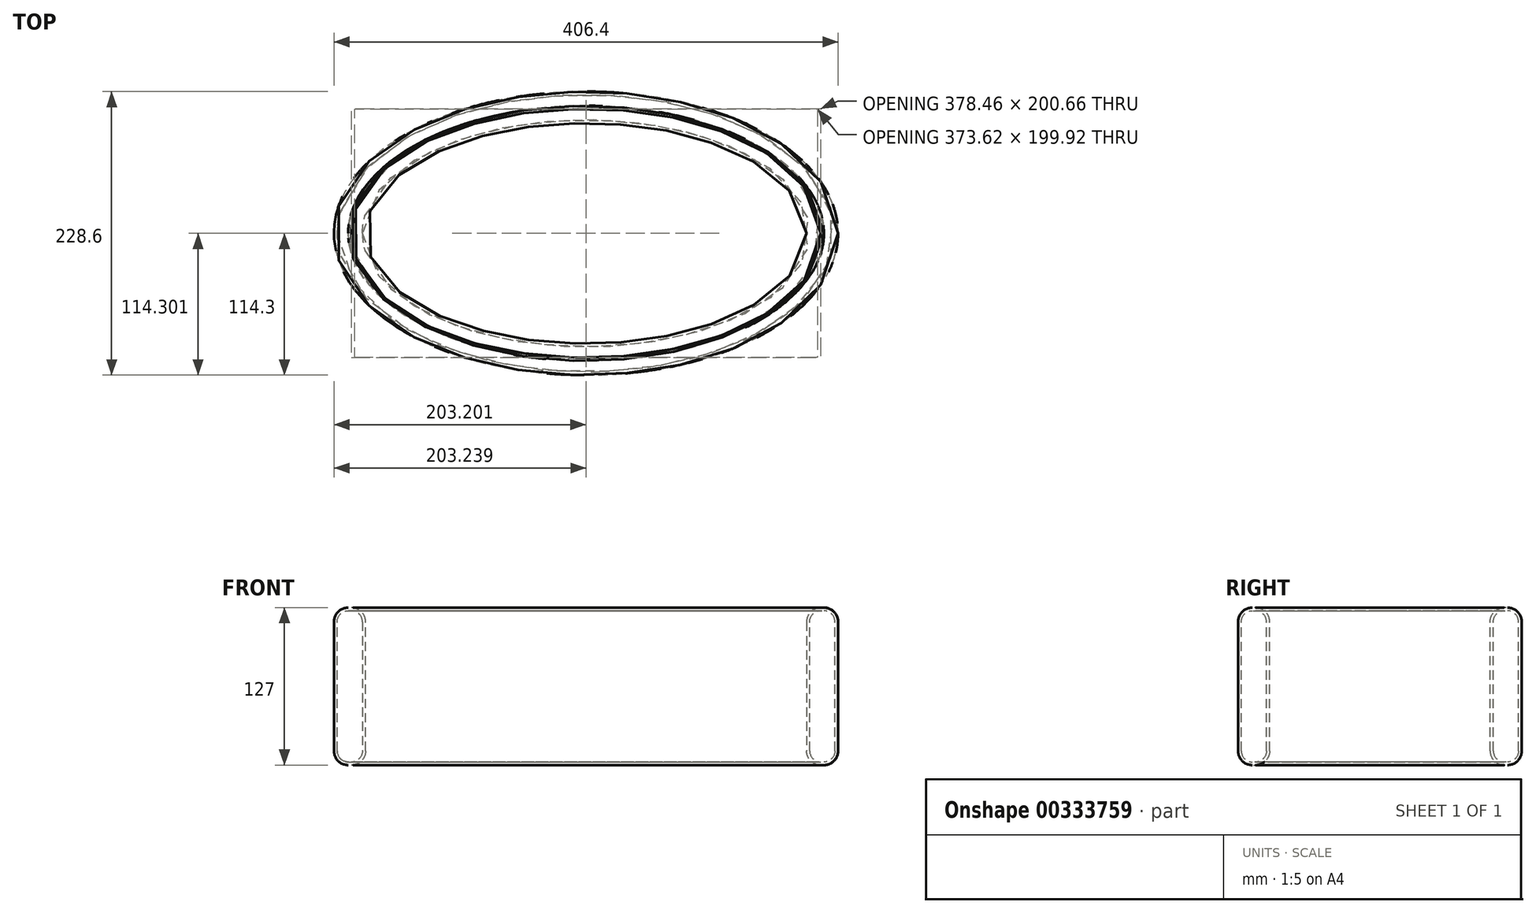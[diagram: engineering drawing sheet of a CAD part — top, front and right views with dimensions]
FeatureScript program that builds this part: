
annotation { "Feature Type Name" : "Feature", "Feature Type Description" : "" }
export const myFeature = defineFeature(function(context is Context, id is Id, definition is map)
    precondition{}
    {
        {
            var Q0;
            Q0=qCreatedBy(makeId("Top.planeOp"),FACE);
            var sketch = newSketch(context, id + "F0", { "sketchPlane" : qUnion([Q0])});
            skEllipse(sketch, "E0", {"center": v(0, 0) * mm, "majorRadius": 177.8 * mm, "minorRadius": 88.9 * mm, "majorAxis": v(1, 0)});
            skEllipse(sketch, "E1", {"center": v(0, 0) * mm, "majorRadius": 203.2 * mm, "minorRadius": 114.3 * mm, "majorAxis": v(1, 0)});
            skSolve(sketch);
        }
        {
            var Q0;
            Q0=makeQuery(id+"F0.imprint","IMPRINT",FACE,{"disambiguationData":[TD([[makeQuery(id+"F0.imprint","IMPRINT",EDGE,{"derivedFrom":sQuery(id+"F0.wireOp",EDGE,"E0")}),-1.0]])]});
            extrude(context, id + "F1", {"entities" : qUnion([Q0]), "depth" : 127 * mm});
        }
        {
            var Q0;
            Q0=makeQuery(id+"F1.opExtrude","CAP_FACE",FACE,{"disambiguationData":[OSD([sQuery(id+"F0.wireOp",EDGE,"E0"),sQuery(id+"F0.wireOp",EDGE,"E1")])],"isStart":false});
            var Q1;
            Q1=makeQuery(id+"F1.opExtrude","CAP_FACE",FACE,{"disambiguationData":[OSD([sQuery(id+"F0.wireOp",EDGE,"E0"),sQuery(id+"F0.wireOp",EDGE,"E1")])],"isStart":true});
            fillet(context, id + "F2", {"entities" : qUnion([Q0, Q1]), "radius" : 11.43 * mm, "tangentPropagation" : true, "allowEdgeOverflow" : false});
        }
        {
            var Q0;
            Q0=makeQuery(id+"F1.opExtrude","SWEPT_FACE",FACE,{"disambiguationData":[OSD([sQuery(id+"F0.wireOp",EDGE,"E1")])]});
            var Q1;
            Q1=makeQuery(id+"F1.opExtrude","SWEPT_BODY",BODY,{"disambiguationData":[OSD([sQuery(id+"F0.wireOp",EDGE,"E0"),sQuery(id+"F0.wireOp",EDGE,"E1")])]});
            shell(context, id + "F3", {"isHollow" : true, "entities" : qUnion([Q0]), "parts" : qUnion([Q1]), "thickness" : 2.54 * mm});
        }
    });
